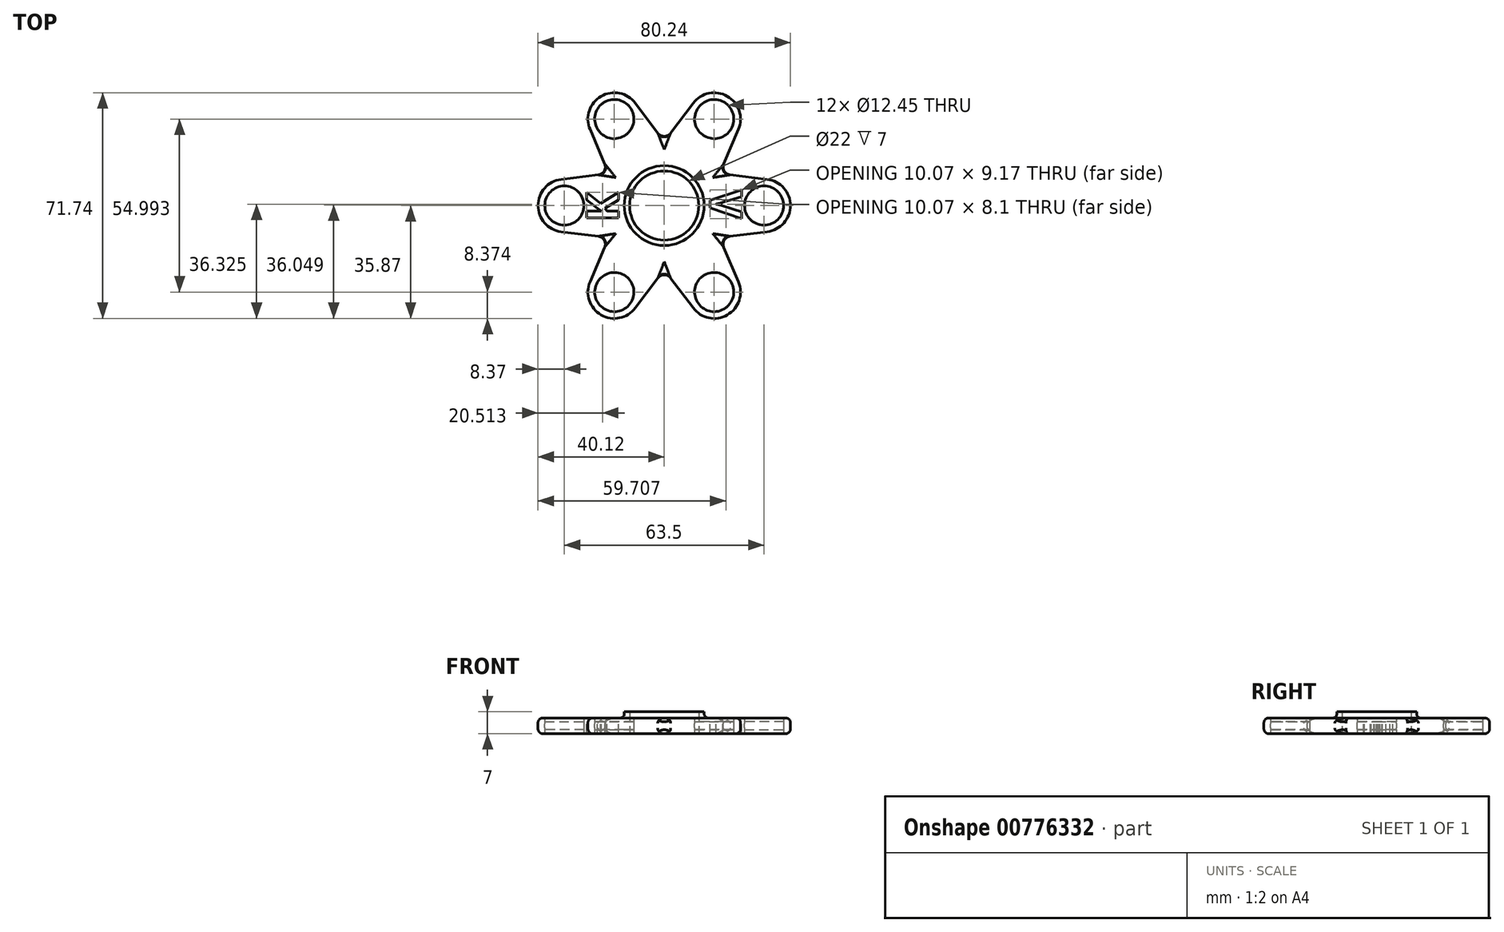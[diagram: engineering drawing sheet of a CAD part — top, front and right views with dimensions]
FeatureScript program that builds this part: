
annotation { "Feature Type Name" : "Feature", "Feature Type Description" : "" }
export const myFeature = defineFeature(function(context is Context, id is Id, definition is map)
    precondition{}
    {
        {
            var Q0;
            Q0=qCreatedBy(makeId("Top.planeOp"),FACE);
            var sketch = newSketch(context, id + "F0", { "sketchPlane" : qUnion([Q0])});
            skCircle(sketch, "E0", {"center": v(0, 0) * mm, "radius": 12.7 * mm});
            skCircle(sketch, "E1", {"center": v(0, 0) * mm, "radius": 11 * mm});
            skSolve(sketch);
        }
        {
            var Q0;
            Q0=makeQuery(id+"F0.imprint","IMPRINT",FACE,{"disambiguationData":[TD([[makeQuery(id+"F0.imprint","IMPRINT",EDGE,{"derivedFrom":sQuery(id+"F0.wireOp",EDGE,"E0")}),1.0]])]});
            extrude(context, id + "F1", {"entities" : qUnion([Q0]), "depth" : 7 * mm, "offsetDistance" : 25.4 * mm});
        }
        {
            var Q0;
            Q0=qCreatedBy(makeId("Top.planeOp"),FACE);
            cPlane(context, id + "F2", {"entities" : qUnion([Q0]), "cplaneType" : CPlaneType.OFFSET, "offset" : 2.5 * mm, "width" : 152.4 * mm, "height" : 152.4 * mm});
        }
        {
            var Q0;
            Q0=qCreatedBy(id+"F2.planeOp",FACE);
            var sketch = newSketch(context, id + "F3", { "sketchPlane" : qUnion([Q0])});
            skArc(sketch, "E2", {"start": v(-32.77, 8.31) * mm, "mid": v(-40.12, 0) * mm, "end": v(-32.77, -8.31) * mm});
            skLineSegment(sketch, "E3", {"start": v(-32.77, 8.31) * mm, "end": v(0, 12.35) * mm});
            skLineSegment(sketch, "E4.MirrorCS", {"start": v(-32.77, -8.31) * mm, "end": v(0, -12.35) * mm});
            skLineSegment(sketch, "E5", {"start": v(0, 12.35) * mm, "end": v(0, 11.32) * mm});
            skArc(sketch, "E6", {"start": v(0, 11.32) * mm, "mid": v(-11.32, 0) * mm, "end": v(0, -11.32) * mm});
            skLineSegment(sketch, "E7.trimOffspring", {"start": v(0, -11.32) * mm, "end": v(0, -12.35) * mm});
            skArc(sketch, "E8", {"start": v(-31.75, 6.35) * mm, "mid": v(-38.1, 0) * mm, "end": v(-31.75, -6.35) * mm});
            skLineSegment(sketch, "E9", {"start": v(-31.75, 6.35) * mm, "end": v(-31.75, -6.35) * mm});
            skCircle(sketch, "E10", {"center": v(-31.75, 0) * mm, "radius": 6.22 * mm});
            skSolve(sketch);
        }
        {
            var Q0;
            Q0=makeQuery(id+"F3.imprint","IMPRINT",FACE,{"disambiguationData":[TD([[makeQuery(id+"F3.imprint","IMPRINT",EDGE,{"derivedFrom":sQuery(id+"F3.wireOp",EDGE,"E2")}),1.0]])]});
            var Q1;
            {var subQ0=sQuery(id+"F3.wireOp",EDGE,"E8");Q1=makeQuery(id+"F3.imprint","IMPRINT",FACE,{"disambiguationData":[TD([[makeQuery(id+"F3.imprint","IMPRINT",EDGE,{"derivedFrom":subQ0}),1.0]])]});}
            extrude(context, id + "F4", {"entities" : qUnion([Q0, Q1]), "endBound" : BoundingType.SYMMETRIC, "depth" : 5 * mm, "offsetDistance" : 25.4 * mm});
        }
        {
            var Q0;
            Q0=qCreatedBy(makeId("Front.planeOp"),FACE);
            var sketch = newSketch(context, id + "F5", { "sketchPlane" : qUnion([Q0])});
            skLineSegment(sketch, "E11", {"start": v(0, 0) * mm, "end": v(0, 41) * mm, "construction": true});
            skSolve(sketch);
        }
        {
            var Q0;
            Q0=makeQuery(id+"F3.imprint","IMPRINT",FACE,{"disambiguationData":[TD([[makeQuery(id+"F3.imprint","IMPRINT",EDGE,{"derivedFrom":sQuery(id+"F3.wireOp",EDGE,"E8")}),1.0]])]});
            var Q1;
            Q1=sQuery(id+"F3.wireOp",EDGE,"E9");
            revolve(context, id + "F6", {"operationType" : NewBodyOperationType.REMOVE, "surfaceOperationType" : NewSurfaceOperationType.NEW, "entities" : qUnion([Q0]), "axis" : qUnion([Q1]), "revolveType" : RevolveType.FULL, "oppositeDirection" : true});
        }
        {
            var Q0;
            Q0=makeQuery(id+"F4.opExtrude","SWEPT_BODY",BODY,{"disambiguationData":[OSD([sQuery(id+"F3.wireOp",EDGE,"E2"),sQuery(id+"F3.wireOp",EDGE,"E3"),sQuery(id+"F3.wireOp",EDGE,"E4.MirrorCS"),sQuery(id+"F3.wireOp",EDGE,"E5"),sQuery(id+"F3.wireOp",EDGE,"gVdO0x3I-Yq7t-95zV-3Q7Q-V35kwEtAvBfn"),sQuery(id+"F3.wireOp",EDGE,"E6"),sQuery(id+"F3.wireOp",EDGE,"E7.trimOffspring")])]});
            var Q1;
            Q1=sQuery(id+"F5.wireOp",EDGE,"E11");
            circularPattern(context, id + "F7", {"entities" : qUnion([Q0]), "axis" : qUnion([Q1]), "angle" : 360 * degree, "instanceCount" : 6, "equalSpace" : true});
        }
        {
            var Q0;
            Q0=makeQuery(id+"F1.opExtrude","SWEPT_BODY",BODY,{"disambiguationData":[OSD([sQuery(id+"F0.wireOp",EDGE,"E0"),sQuery(id+"F0.wireOp",EDGE,"E1")])]});
            var Q1;
            Q1=makeQuery(id+"F4.opExtrude","SWEPT_BODY",BODY,{"disambiguationData":[OSD([sQuery(id+"F3.wireOp",EDGE,"E2"),sQuery(id+"F3.wireOp",EDGE,"E3"),sQuery(id+"F3.wireOp",EDGE,"E4.MirrorCS"),sQuery(id+"F3.wireOp",EDGE,"E5"),sQuery(id+"F3.wireOp",EDGE,"gVdO0x3I-Yq7t-95zV-3Q7Q-V35kwEtAvBfn"),sQuery(id+"F3.wireOp",EDGE,"E6"),sQuery(id+"F3.wireOp",EDGE,"E7.trimOffspring")])]});
            var Q2;
            Q2=makeQuery(id+"F7.opPattern","COPY",BODY,{"derivedFrom":makeQuery(id+"F4.opExtrude","SWEPT_BODY",BODY,{"disambiguationData":[OSD([sQuery(id+"F3.wireOp",EDGE,"E2"),sQuery(id+"F3.wireOp",EDGE,"E3"),sQuery(id+"F3.wireOp",EDGE,"E4.MirrorCS"),sQuery(id+"F3.wireOp",EDGE,"E5"),sQuery(id+"F3.wireOp",EDGE,"gVdO0x3I-Yq7t-95zV-3Q7Q-V35kwEtAvBfn"),sQuery(id+"F3.wireOp",EDGE,"E6"),sQuery(id+"F3.wireOp",EDGE,"E7.trimOffspring")])]}),"instanceName":"1"});
            var Q3;
            Q3=makeQuery(id+"F7.opPattern","COPY",BODY,{"derivedFrom":makeQuery(id+"F4.opExtrude","SWEPT_BODY",BODY,{"disambiguationData":[OSD([sQuery(id+"F3.wireOp",EDGE,"E2"),sQuery(id+"F3.wireOp",EDGE,"E3"),sQuery(id+"F3.wireOp",EDGE,"E4.MirrorCS"),sQuery(id+"F3.wireOp",EDGE,"E5"),sQuery(id+"F3.wireOp",EDGE,"gVdO0x3I-Yq7t-95zV-3Q7Q-V35kwEtAvBfn"),sQuery(id+"F3.wireOp",EDGE,"E6"),sQuery(id+"F3.wireOp",EDGE,"E7.trimOffspring")])]}),"instanceName":"2"});
            var Q4;
            Q4=makeQuery(id+"F7.opPattern","COPY",BODY,{"derivedFrom":makeQuery(id+"F4.opExtrude","SWEPT_BODY",BODY,{"disambiguationData":[OSD([sQuery(id+"F3.wireOp",EDGE,"E2"),sQuery(id+"F3.wireOp",EDGE,"E3"),sQuery(id+"F3.wireOp",EDGE,"E4.MirrorCS"),sQuery(id+"F3.wireOp",EDGE,"E5"),sQuery(id+"F3.wireOp",EDGE,"gVdO0x3I-Yq7t-95zV-3Q7Q-V35kwEtAvBfn"),sQuery(id+"F3.wireOp",EDGE,"E6"),sQuery(id+"F3.wireOp",EDGE,"E7.trimOffspring")])]}),"instanceName":"3"});
            var Q5;
            Q5=makeQuery(id+"F7.opPattern","COPY",BODY,{"derivedFrom":makeQuery(id+"F4.opExtrude","SWEPT_BODY",BODY,{"disambiguationData":[OSD([sQuery(id+"F3.wireOp",EDGE,"E2"),sQuery(id+"F3.wireOp",EDGE,"E3"),sQuery(id+"F3.wireOp",EDGE,"E4.MirrorCS"),sQuery(id+"F3.wireOp",EDGE,"E5"),sQuery(id+"F3.wireOp",EDGE,"gVdO0x3I-Yq7t-95zV-3Q7Q-V35kwEtAvBfn"),sQuery(id+"F3.wireOp",EDGE,"E6"),sQuery(id+"F3.wireOp",EDGE,"E7.trimOffspring")])]}),"instanceName":"4"});
            var Q6;
            Q6=makeQuery(id+"F7.opPattern","COPY",BODY,{"derivedFrom":makeQuery(id+"F4.opExtrude","SWEPT_BODY",BODY,{"disambiguationData":[OSD([sQuery(id+"F3.wireOp",EDGE,"E2"),sQuery(id+"F3.wireOp",EDGE,"E3"),sQuery(id+"F3.wireOp",EDGE,"E4.MirrorCS"),sQuery(id+"F3.wireOp",EDGE,"E5"),sQuery(id+"F3.wireOp",EDGE,"gVdO0x3I-Yq7t-95zV-3Q7Q-V35kwEtAvBfn"),sQuery(id+"F3.wireOp",EDGE,"E6"),sQuery(id+"F3.wireOp",EDGE,"E7.trimOffspring")])]}),"instanceName":"5"});
            booleanBodies(context, id + "F8", {"operationType" : BooleanOperationType.UNION, "tools" : qUnion([Q0, Q1, Q2, Q3, Q4, Q5, Q6])});
        }
        {
            var Q0;
            Q0=makeQuery(id+"F8.opBoolean","INTERSECT",EDGE,{"derivedFrom":[makeQuery(id+"F1.opExtrude","SWEPT_FACE",FACE,{"disambiguationData":[OSD([sQuery(id+"F0.wireOp",EDGE,"E0")])]}),makeQuery(id+"F7.opPattern","COPY",FACE,{"derivedFrom":makeQuery(id+"F4.opExtrude","CAP_FACE",FACE,{"disambiguationData":[OSD([sQuery(id+"F3.wireOp",EDGE,"E2"),sQuery(id+"F3.wireOp",EDGE,"E3"),sQuery(id+"F3.wireOp",EDGE,"E4.MirrorCS"),sQuery(id+"F3.wireOp",EDGE,"E5"),sQuery(id+"F3.wireOp",EDGE,"gVdO0x3I-Yq7t-95zV-3Q7Q-V35kwEtAvBfn"),sQuery(id+"F3.wireOp",EDGE,"E6"),sQuery(id+"F3.wireOp",EDGE,"E7.trimOffspring")])],"isStart":false}),"instanceName":"1"})]});
            var Q1;
            Q1=makeQuery(id+"F8.opBoolean","INTERSECT",EDGE,{"derivedFrom":[makeQuery(id+"F1.opExtrude","SWEPT_FACE",FACE,{"disambiguationData":[OSD([sQuery(id+"F0.wireOp",EDGE,"E0")])]}),makeQuery(id+"F7.opPattern","COPY",FACE,{"derivedFrom":makeQuery(id+"F4.opExtrude","CAP_FACE",FACE,{"disambiguationData":[OSD([sQuery(id+"F3.wireOp",EDGE,"E2"),sQuery(id+"F3.wireOp",EDGE,"E3"),sQuery(id+"F3.wireOp",EDGE,"E4.MirrorCS"),sQuery(id+"F3.wireOp",EDGE,"E5"),sQuery(id+"F3.wireOp",EDGE,"gVdO0x3I-Yq7t-95zV-3Q7Q-V35kwEtAvBfn"),sQuery(id+"F3.wireOp",EDGE,"E6"),sQuery(id+"F3.wireOp",EDGE,"E7.trimOffspring")])],"isStart":true}),"instanceName":"1"})]});
            fillet(context, id + "F9", {"entities" : qUnion([Q0, Q1]), "radius" : 1.27 * mm, "tangentPropagation" : true, "allowEdgeOverflow" : false});
        }
        {
            var Q0;
            Q0=makeQuery(id+"F4.opExtrude","CAP_EDGE",EDGE,{"disambiguationData":[OSD([sQuery(id+"F3.wireOp",EDGE,"E4.MirrorCS")])],"isStart":false});
            var Q1;
            Q1=makeQuery(id+"F7.opPattern","COPY",EDGE,{"derivedFrom":makeQuery(id+"F4.opExtrude","CAP_EDGE",EDGE,{"disambiguationData":[OSD([sQuery(id+"F3.wireOp",EDGE,"E3")])],"isStart":false}),"instanceName":"1"});
            var Q2;
            Q2=makeQuery(id+"F7.opPattern","COPY",EDGE,{"derivedFrom":makeQuery(id+"F4.opExtrude","CAP_EDGE",EDGE,{"disambiguationData":[OSD([sQuery(id+"F3.wireOp",EDGE,"E2")])],"isStart":false}),"instanceName":"1"});
            var Q3;
            Q3=makeQuery(id+"F7.opPattern","COPY",EDGE,{"derivedFrom":makeQuery(id+"F4.opExtrude","CAP_EDGE",EDGE,{"disambiguationData":[OSD([sQuery(id+"F3.wireOp",EDGE,"E4.MirrorCS")])],"isStart":false}),"instanceName":"1"});
            var Q4;
            Q4=makeQuery(id+"F7.opPattern","COPY",EDGE,{"derivedFrom":makeQuery(id+"F4.opExtrude","CAP_EDGE",EDGE,{"disambiguationData":[OSD([sQuery(id+"F3.wireOp",EDGE,"E3")])],"isStart":false}),"instanceName":"2"});
            var Q5;
            Q5=makeQuery(id+"F7.opPattern","COPY",EDGE,{"derivedFrom":makeQuery(id+"F4.opExtrude","CAP_EDGE",EDGE,{"disambiguationData":[OSD([sQuery(id+"F3.wireOp",EDGE,"E2")])],"isStart":false}),"instanceName":"2"});
            var Q6;
            Q6=makeQuery(id+"F7.opPattern","COPY",EDGE,{"derivedFrom":makeQuery(id+"F4.opExtrude","CAP_EDGE",EDGE,{"disambiguationData":[OSD([sQuery(id+"F3.wireOp",EDGE,"E4.MirrorCS")])],"isStart":false}),"instanceName":"2"});
            var Q7;
            Q7=makeQuery(id+"F7.opPattern","COPY",EDGE,{"derivedFrom":makeQuery(id+"F4.opExtrude","CAP_EDGE",EDGE,{"disambiguationData":[OSD([sQuery(id+"F3.wireOp",EDGE,"E3")])],"isStart":false}),"instanceName":"3"});
            var Q8;
            Q8=makeQuery(id+"F7.opPattern","COPY",EDGE,{"derivedFrom":makeQuery(id+"F4.opExtrude","CAP_EDGE",EDGE,{"disambiguationData":[OSD([sQuery(id+"F3.wireOp",EDGE,"E2")])],"isStart":false}),"instanceName":"3"});
            var Q9;
            Q9=makeQuery(id+"F7.opPattern","COPY",EDGE,{"derivedFrom":makeQuery(id+"F4.opExtrude","CAP_EDGE",EDGE,{"disambiguationData":[OSD([sQuery(id+"F3.wireOp",EDGE,"E4.MirrorCS")])],"isStart":false}),"instanceName":"3"});
            var Q10;
            Q10=makeQuery(id+"F7.opPattern","COPY",EDGE,{"derivedFrom":makeQuery(id+"F4.opExtrude","CAP_EDGE",EDGE,{"disambiguationData":[OSD([sQuery(id+"F3.wireOp",EDGE,"E3")])],"isStart":false}),"instanceName":"4"});
            var Q11;
            Q11=makeQuery(id+"F7.opPattern","COPY",EDGE,{"derivedFrom":makeQuery(id+"F4.opExtrude","CAP_EDGE",EDGE,{"disambiguationData":[OSD([sQuery(id+"F3.wireOp",EDGE,"E4.MirrorCS")])],"isStart":false}),"instanceName":"4"});
            var Q12;
            Q12=makeQuery(id+"F7.opPattern","COPY",EDGE,{"derivedFrom":makeQuery(id+"F4.opExtrude","CAP_EDGE",EDGE,{"disambiguationData":[OSD([sQuery(id+"F3.wireOp",EDGE,"E2")])],"isStart":false}),"instanceName":"4"});
            var Q13;
            Q13=makeQuery(id+"F7.opPattern","COPY",EDGE,{"derivedFrom":makeQuery(id+"F4.opExtrude","CAP_EDGE",EDGE,{"disambiguationData":[OSD([sQuery(id+"F3.wireOp",EDGE,"E3")])],"isStart":false}),"instanceName":"5"});
            var Q14;
            Q14=makeQuery(id+"F7.opPattern","COPY",EDGE,{"derivedFrom":makeQuery(id+"F4.opExtrude","CAP_EDGE",EDGE,{"disambiguationData":[OSD([sQuery(id+"F3.wireOp",EDGE,"E4.MirrorCS")])],"isStart":false}),"instanceName":"5"});
            var Q15;
            Q15=makeQuery(id+"F7.opPattern","COPY",EDGE,{"derivedFrom":makeQuery(id+"F4.opExtrude","CAP_EDGE",EDGE,{"disambiguationData":[OSD([sQuery(id+"F3.wireOp",EDGE,"E2")])],"isStart":false}),"instanceName":"5"});
            var Q16;
            Q16=makeQuery(id+"F4.opExtrude","CAP_EDGE",EDGE,{"disambiguationData":[OSD([sQuery(id+"F3.wireOp",EDGE,"E3")])],"isStart":false});
            var Q17;
            Q17=makeQuery(id+"F4.opExtrude","CAP_EDGE",EDGE,{"disambiguationData":[OSD([sQuery(id+"F3.wireOp",EDGE,"E2")])],"isStart":false});
            var Q18;
            Q18=makeQuery(id+"F4.opExtrude","CAP_EDGE",EDGE,{"disambiguationData":[OSD([sQuery(id+"F3.wireOp",EDGE,"E4.MirrorCS")])],"isStart":true});
            var Q19;
            Q19=makeQuery(id+"F7.opPattern","COPY",EDGE,{"derivedFrom":makeQuery(id+"F4.opExtrude","CAP_EDGE",EDGE,{"disambiguationData":[OSD([sQuery(id+"F3.wireOp",EDGE,"E3")])],"isStart":true}),"instanceName":"1"});
            var Q20;
            Q20=makeQuery(id+"F7.opPattern","COPY",EDGE,{"derivedFrom":makeQuery(id+"F4.opExtrude","CAP_EDGE",EDGE,{"disambiguationData":[OSD([sQuery(id+"F3.wireOp",EDGE,"E3")])],"isStart":true}),"instanceName":"2"});
            var Q21;
            Q21=makeQuery(id+"F7.opPattern","COPY",EDGE,{"derivedFrom":makeQuery(id+"F4.opExtrude","CAP_EDGE",EDGE,{"disambiguationData":[OSD([sQuery(id+"F3.wireOp",EDGE,"E3")])],"isStart":true}),"instanceName":"3"});
            var Q22;
            Q22=makeQuery(id+"F7.opPattern","COPY",EDGE,{"derivedFrom":makeQuery(id+"F4.opExtrude","CAP_EDGE",EDGE,{"disambiguationData":[OSD([sQuery(id+"F3.wireOp",EDGE,"E3")])],"isStart":true}),"instanceName":"4"});
            var Q23;
            Q23=makeQuery(id+"F7.opPattern","COPY",EDGE,{"derivedFrom":makeQuery(id+"F4.opExtrude","CAP_EDGE",EDGE,{"disambiguationData":[OSD([sQuery(id+"F3.wireOp",EDGE,"E3")])],"isStart":true}),"instanceName":"5"});
            fillet(context, id + "F10", {"entities" : qUnion([Q0, Q1, Q2, Q3, Q4, Q5, Q6, Q7, Q8, Q9, Q10, Q11, Q12, Q13, Q14, Q15, Q16, Q17, Q18, Q19, Q20, Q21, Q22, Q23]), "radius" : 1.52 * mm, "tangentPropagation" : true, "allowEdgeOverflow" : false});
        }
        {
            var Q0;
            Q0=makeQuery(id+"F8.opBoolean","INTERSECT",EDGE,{"derivedFrom":[makeQuery(id+"F4.opExtrude","SWEPT_FACE",FACE,{"disambiguationData":[OSD([sQuery(id+"F3.wireOp",EDGE,"E4.MirrorCS")])]}),makeQuery(id+"F7.opPattern","COPY",FACE,{"derivedFrom":makeQuery(id+"F4.opExtrude","SWEPT_FACE",FACE,{"disambiguationData":[OSD([sQuery(id+"F3.wireOp",EDGE,"E3")])]}),"instanceName":"1"})]});
            var Q1;
            Q1=makeQuery(id+"F10.opFillet","BLEND_EDGE",EDGE,{"blendedFrom":[makeQuery(id+"F7.opPattern","COPY",EDGE,{"derivedFrom":makeQuery(id+"F4.opExtrude","CAP_EDGE",EDGE,{"disambiguationData":[OSD([sQuery(id+"F3.wireOp",EDGE,"E4.MirrorCS")])],"isStart":false}),"instanceName":"1"}),makeQuery(id+"F7.opPattern","COPY",EDGE,{"derivedFrom":makeQuery(id+"F4.opExtrude","CAP_EDGE",EDGE,{"disambiguationData":[OSD([sQuery(id+"F3.wireOp",EDGE,"E3")])],"isStart":false}),"instanceName":"2"})],"blendedInto":[]});
            var Q2;
            Q2=makeQuery(id+"F10.opFillet","BLEND_EDGE",EDGE,{"blendedFrom":[makeQuery(id+"F7.opPattern","COPY",EDGE,{"derivedFrom":makeQuery(id+"F4.opExtrude","CAP_EDGE",EDGE,{"disambiguationData":[OSD([sQuery(id+"F3.wireOp",EDGE,"E4.MirrorCS")])],"isStart":false}),"instanceName":"2"}),makeQuery(id+"F7.opPattern","COPY",EDGE,{"derivedFrom":makeQuery(id+"F4.opExtrude","CAP_EDGE",EDGE,{"disambiguationData":[OSD([sQuery(id+"F3.wireOp",EDGE,"E3")])],"isStart":false}),"instanceName":"3"})],"blendedInto":[]});
            var Q3;
            Q3=makeQuery(id+"F10.opFillet","BLEND_EDGE",EDGE,{"blendedFrom":[makeQuery(id+"F4.opExtrude","CAP_EDGE",EDGE,{"disambiguationData":[OSD([sQuery(id+"F3.wireOp",EDGE,"E3")])],"isStart":false}),makeQuery(id+"F7.opPattern","COPY",EDGE,{"derivedFrom":makeQuery(id+"F4.opExtrude","CAP_EDGE",EDGE,{"disambiguationData":[OSD([sQuery(id+"F3.wireOp",EDGE,"E4.MirrorCS")])],"isStart":false}),"instanceName":"5"})],"blendedInto":[]});
            var Q4;
            Q4=makeQuery(id+"F10.opFillet","BLEND_EDGE",EDGE,{"blendedFrom":[makeQuery(id+"F7.opPattern","COPY",EDGE,{"derivedFrom":makeQuery(id+"F4.opExtrude","CAP_EDGE",EDGE,{"disambiguationData":[OSD([sQuery(id+"F3.wireOp",EDGE,"E4.MirrorCS")])],"isStart":false}),"instanceName":"4"}),makeQuery(id+"F7.opPattern","COPY",EDGE,{"derivedFrom":makeQuery(id+"F4.opExtrude","CAP_EDGE",EDGE,{"disambiguationData":[OSD([sQuery(id+"F3.wireOp",EDGE,"E3")])],"isStart":false}),"instanceName":"5"})],"blendedInto":[]});
            var Q5;
            Q5=makeQuery(id+"F10.opFillet","BLEND_EDGE",EDGE,{"blendedFrom":[makeQuery(id+"F7.opPattern","COPY",EDGE,{"derivedFrom":makeQuery(id+"F4.opExtrude","CAP_EDGE",EDGE,{"disambiguationData":[OSD([sQuery(id+"F3.wireOp",EDGE,"E4.MirrorCS")])],"isStart":false}),"instanceName":"3"}),makeQuery(id+"F7.opPattern","COPY",EDGE,{"derivedFrom":makeQuery(id+"F4.opExtrude","CAP_EDGE",EDGE,{"disambiguationData":[OSD([sQuery(id+"F3.wireOp",EDGE,"E3")])],"isStart":false}),"instanceName":"4"})],"blendedInto":[]});
            fillet(context, id + "F11", {"entities" : qUnion([Q0, Q1, Q2, Q3, Q4, Q5]), "radius" : 2.54 * mm, "tangentPropagation" : true, "allowEdgeOverflow" : false});
        }
        {
            var Q0;
            Q0=qCreatedBy(makeId("Top.planeOp"),FACE);
            var sketch = newSketch(context, id + "F12", { "sketchPlane" : qUnion([Q0])});
            skText(sketch, "E12", { "text": "K", "fontName": "OpenSans-Bold.ttf"});
            skText(sketch, "E13", { "text": "V", "fontName": "OpenSans-Bold.ttf"});
            const initialGuessF12  = {"E12": [-0.01457, -0.00514, 0, 1, 0.01016], "E13": [0.01455, 0.00504, 0, -1, 0.01016]};
            skSetInitialGuess(sketch, initialGuessF12);
            skSolve(sketch);
        }
        {
            var Q0;
            Q0=qSketchRegion(id+"F12",true);
            extrude(context, id + "F13", {"entities" : qUnion([Q0]), "operationType" : NewBodyOperationType.REMOVE, "endBound" : BoundingType.SYMMETRIC, "oppositeDirection" : true, "depth" : 25.4 * mm, "offsetDistance" : 25.4 * mm});
        }
    });
